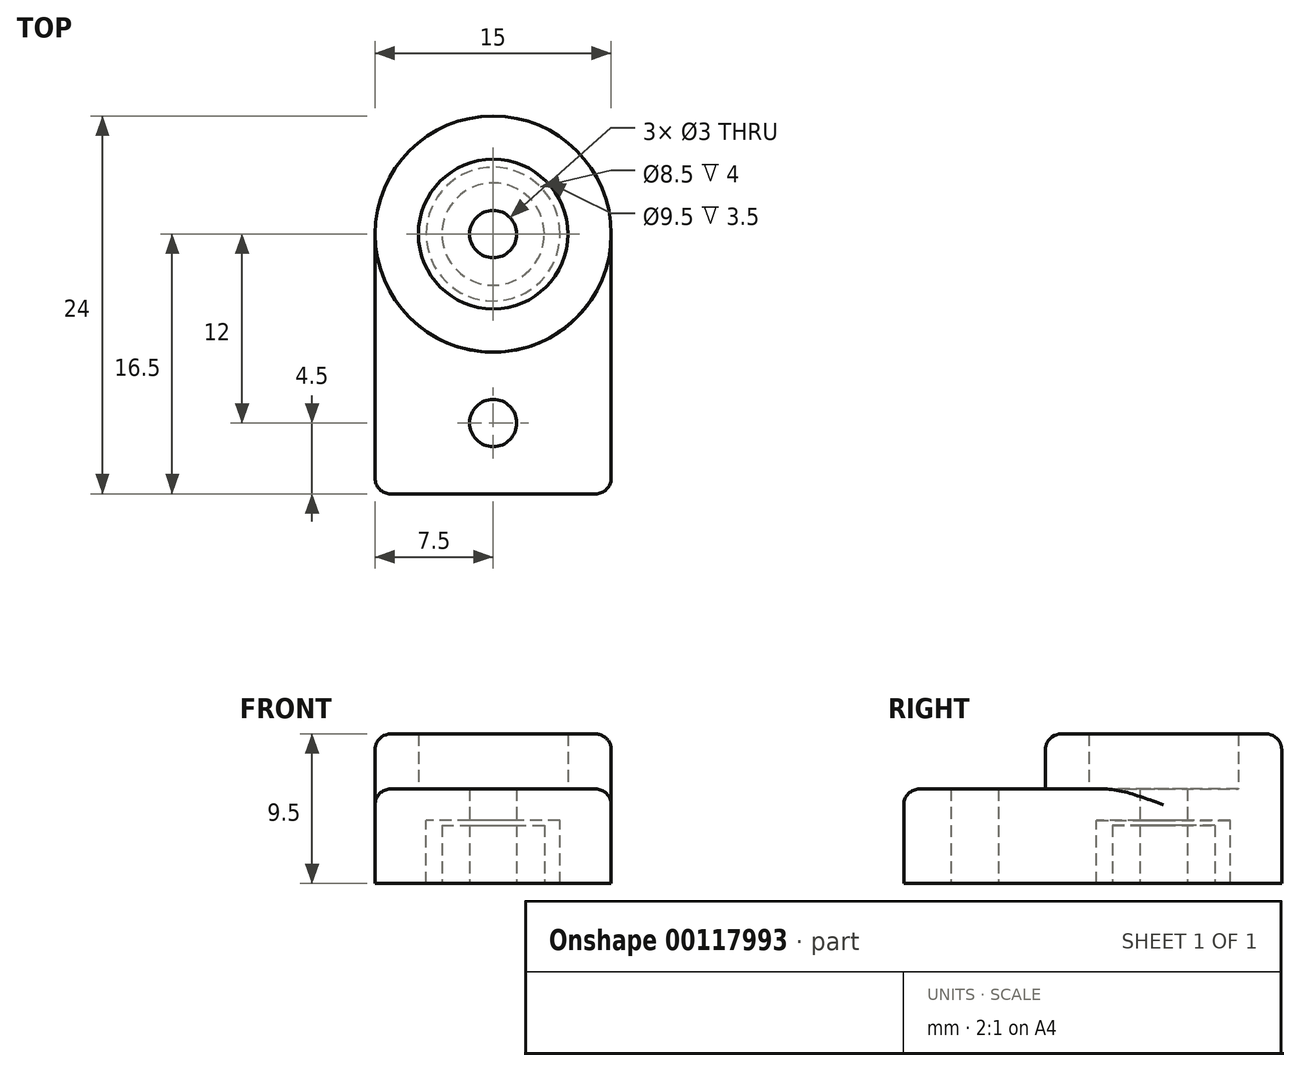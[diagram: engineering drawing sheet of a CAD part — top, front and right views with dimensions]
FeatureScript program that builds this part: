
annotation { "Feature Type Name" : "Feature", "Feature Type Description" : "" }
export const myFeature = defineFeature(function(context is Context, id is Id, definition is map)
    precondition{}
    {
        {
            var Q0;
            Q0=qCreatedBy(makeId("Top.planeOp"),FACE);
            var sketch = newSketch(context, id + "F0", { "sketchPlane" : qUnion([Q0])});
            skCircle(sketch, "E0", {"center": v(0, 36.5) * mm, "radius": 7.5 * mm});
            skLineSegment(sketch, "E1", {"start": v(-7.5, 36.5) * mm, "end": v(-7.5, 20) * mm});
            skLineSegment(sketch, "E2", {"start": v(-7.5, 20) * mm, "end": v(7.5, 20) * mm});
            skLineSegment(sketch, "E3", {"start": v(7.5, 20) * mm, "end": v(7.5, 36.5) * mm});
            skLineSegment(sketch, "E4", {"start": v(0, 0) * mm, "end": v(0, 36.5) * mm, "construction": true});
            skCircle(sketch, "E5", {"center": v(0, 24.5) * mm, "radius": 1.5 * mm});
            skCircle(sketch, "E6", {"center": v(0, 36.5) * mm, "radius": 4.75 * mm});
            skCircle(sketch, "E7", {"center": v(0, 36.5) * mm, "radius": 1.5 * mm});
            skCircle(sketch, "E8", {"center": v(0, 36.5) * mm, "radius": 4.25 * mm});
            skSolve(sketch);
        }
        {
            var Q0;
            {var subQ1=sQuery(id+"F0.wireOp",EDGE,"E1");Q0=makeQuery(id+"F0.imprint","IMPRINT",FACE,{"disambiguationData":[TD([[makeQuery(id+"F0.imprint","IMPRINT",EDGE,{"derivedFrom":subQ1}),1.0]])]});}
            var Q1;
            Q1=makeQuery(id+"F0.imprint","IMPRINT",FACE,{"disambiguationData":[TD([[makeQuery(id+"F0.imprint","IMPRINT",EDGE,{"derivedFrom":sQuery(id+"F0.wireOp",EDGE,"E6")}),-1.0]])]});
            var Q2;
            Q2=makeQuery(id+"F0.imprint","IMPRINT",FACE,{"disambiguationData":[TD([[makeQuery(id+"F0.imprint","IMPRINT",EDGE,{"derivedFrom":sQuery(id+"F0.wireOp",EDGE,"E6")}),1.0]])]});
            var Q3;
            Q3=makeQuery(id+"F0.imprint","IMPRINT",FACE,{"disambiguationData":[TD([[makeQuery(id+"F0.imprint","IMPRINT",EDGE,{"derivedFrom":sQuery(id+"F0.wireOp",EDGE,"E7")}),-1.0]])]});
            extrude(context, id + "F1", {"entities" : qUnion([Q0, Q1, Q2, Q3]), "depth" : 2 * mm});
        }
        {
            var Q0;
            {var subQ1=sQuery(id+"F0.wireOp",EDGE,"E1");Q0=makeQuery(id+"F0.imprint","IMPRINT",FACE,{"disambiguationData":[TD([[makeQuery(id+"F0.imprint","IMPRINT",EDGE,{"derivedFrom":subQ1}),1.0]])]});}
            var Q1;
            Q1=makeQuery(id+"F0.imprint","IMPRINT",FACE,{"disambiguationData":[TD([[makeQuery(id+"F0.imprint","IMPRINT",EDGE,{"derivedFrom":sQuery(id+"F0.wireOp",EDGE,"E6")}),-1.0]])]});
            var Q2;
            Q2=makeQuery(id+"F0.imprint","IMPRINT",FACE,{"disambiguationData":[TD([[makeQuery(id+"F0.imprint","IMPRINT",EDGE,{"derivedFrom":sQuery(id+"F0.wireOp",EDGE,"E6")}),1.0]])]});
            extrude(context, id + "F2", {"entities" : qUnion([Q0, Q1, Q2]), "operationType" : NewBodyOperationType.ADD, "oppositeDirection" : true, "depth" : 4 * mm});
        }
        {
            var Q0;
            Q0=makeQuery(id+"F1.opExtrude","CAP_FACE",FACE,{"disambiguationData":[OSD([sQuery(id+"F0.wireOp",EDGE,"E0"),sQuery(id+"F0.wireOp",EDGE,"E1"),sQuery(id+"F0.wireOp",EDGE,"E2"),sQuery(id+"F0.wireOp",EDGE,"E3"),sQuery(id+"F0.wireOp",EDGE,"E5"),sQuery(id+"F0.wireOp",EDGE,"E7")])],"isStart":false});
            var sketch = newSketch(context, id + "F3", { "sketchPlane" : qUnion([Q0])});
            skCircle(sketch, "E9.0", {"center": v(0, 36.5) * mm, "radius": 7.5 * mm});
            skCircle(sketch, "E9.1", {"center": v(0, 36.5) * mm, "radius": 4.75 * mm});
            skSolve(sketch);
        }
        {
            var Q0;
            Q0=makeQuery(id+"F3.imprint","IMPRINT",FACE,{"disambiguationData":[TD([[makeQuery(id+"F3.imprint","IMPRINT",EDGE,{"derivedFrom":sQuery(id+"F3.wireOp",EDGE,"E9.1")}),-1.0]])]});
            extrude(context, id + "F4", {"entities" : qUnion([Q0]), "operationType" : NewBodyOperationType.ADD, "depth" : 3.5 * mm});
        }
        {
            var Q0;
            {var subQ0=sQuery(id+"F0.wireOp",EDGE,"E3");var subQ1=sQuery(id+"F0.wireOp",EDGE,"E2");Q0=makeQuery(id+"F2.boolean.opBoolean","MERGE",EDGE,{"derivedFrom":[makeQuery(id+"F1.opExtrude","SWEPT_EDGE",EDGE,{"disambiguationData":[OSD([subQ1,subQ0])]}),makeQuery(id+"F2.opExtrude","SWEPT_EDGE",EDGE,{"disambiguationData":[OSD([subQ1,subQ0])]})]});}
            var Q1;
            Q1=makeQuery(id+"F1.opExtrude","CAP_EDGE",EDGE,{"disambiguationData":[OSD([sQuery(id+"F0.wireOp",EDGE,"E3")])],"isStart":false});
            var Q2;
            Q2=makeQuery(id+"F1.opExtrude","CAP_EDGE",EDGE,{"disambiguationData":[OSD([sQuery(id+"F0.wireOp",EDGE,"E2")])],"isStart":false});
            var Q3;
            Q3=makeQuery(id+"F1.opExtrude","CAP_EDGE",EDGE,{"disambiguationData":[OSD([sQuery(id+"F0.wireOp",EDGE,"E1")])],"isStart":false});
            var Q4;
            {var subQ0=sQuery(id+"F0.wireOp",EDGE,"E2");var subQ1=sQuery(id+"F0.wireOp",EDGE,"E1");Q4=makeQuery(id+"F2.boolean.opBoolean","MERGE",EDGE,{"derivedFrom":[makeQuery(id+"F1.opExtrude","SWEPT_EDGE",EDGE,{"disambiguationData":[OSD([subQ1,subQ0])]}),makeQuery(id+"F2.opExtrude","SWEPT_EDGE",EDGE,{"disambiguationData":[OSD([subQ1,subQ0])]})]});}
            var Q5;
            Q5=makeQuery(id+"F4.opExtrude","CAP_EDGE",EDGE,{"disambiguationData":[OSD([sQuery(id+"F3.wireOp",EDGE,"E9.0")])],"isStart":false});
            fillet(context, id + "F5", {"entities" : qUnion([Q0, Q1, Q2, Q3, Q4, Q5]), "radius" : 1 * mm, "tangentPropagation" : true, "allowEdgeOverflow" : false});
        }
        {
            var Q0;
            Q0=makeQuery(id+"F2.opExtrude","CAP_FACE",FACE,{"disambiguationData":[OSD([sQuery(id+"F0.wireOp",EDGE,"E0"),sQuery(id+"F0.wireOp",EDGE,"E1"),sQuery(id+"F0.wireOp",EDGE,"E2"),sQuery(id+"F0.wireOp",EDGE,"E3"),sQuery(id+"F0.wireOp",EDGE,"E5"),sQuery(id+"F0.wireOp",EDGE,"E8")])],"isStart":false});
            var sketch = newSketch(context, id + "F6", { "sketchPlane" : qUnion([Q0])});
            skCircle(sketch, "E10.0", {"center": v(0, -36.5) * mm, "radius": 4.25 * mm, "construction": true});
            skCircle(sketch, "E11", {"center": v(0, -36.5) * mm, "radius": 3.25 * mm});
            skCircle(sketch, "E12", {"center": v(0, -36.5) * mm, "radius": 1.5 * mm});
            skSolve(sketch);
        }
        {
            var Q0;
            Q0=makeQuery(id+"F6.imprint","IMPRINT",FACE,{"disambiguationData":[TD([[makeQuery(id+"F6.imprint","IMPRINT",EDGE,{"derivedFrom":sQuery(id+"F6.wireOp",EDGE,"E11")}),1.0]])]});
            extrude(context, id + "F7", {"entities" : qUnion([Q0]), "operationType" : NewBodyOperationType.ADD, "oppositeDirection" : true, "depth" : 3.7 * mm});
        }
    });
